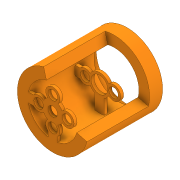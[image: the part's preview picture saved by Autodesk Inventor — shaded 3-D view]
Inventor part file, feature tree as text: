
AUTODESK INVENTOR PART (.ipt)
format: ipt  version: 2020 (Build 240168000, 168)  size: 354,816 bytes
history: native  units: in
note: dims shown in document units (in); Inventor stores cm internally (conversion verified against a paired STEP export)
features: extrude x7, sketch x7, projected_geometry x3, chamfer x1
ambient origin geometry x8: Origin, YZ Plane, XZ Plane, XY Plane, X Axis, Y Axis, Z Axis, Center Point
bodies: Solid1 (feature_tree)
feature tree (18):
  extrude  "Extrusion1"  Depth=2.0472in
  extrude  "Extrusion2"  Depth=1.6535in
  chamfer  "Chamfer1"  Distance=0.5512in
  extrude  "Extrusion3"  Depth=0.2756in
  extrude  "Extrusion4"  Depth=0.2756in TaperAngle=0.0deg
  extrude  "Extrusion5"  Depth=0.315in
  extrude  "Extrusion6"  Depth=0.315in
  extrude  "Extrusion7"  Depth=0.315in
  sketch  "Sketch1"  dims[d0=2.3622in d1=2.0472in]
  sketch  "Sketch2"  dims[d2=0.2756in d3=0.0in d4=1.6535in d5=0.5512in d6=0.0in]
  sketch  "Sketch3"  dims[d7=0.2756in d8=0.125in d9=0.0137in d10=0.0157in]
  sketch  "Sketch5"  dims[d11=4.7244in d13=360.0deg d15=0.2756in d16=0.0in]
  sketch  "Sketch6"  dims[d17=0.5512in d19=0.315in]
  projected_geometry  "Projected Loop1"
  sketch  "Sketch7"  dims[d20=0.315in d21=0.4724in]
  projected_geometry  "Projected Loop2"
  sketch  "Sketch8"  dims[d22=0.4724in d23=0.0787in d24=0.0787in d25=0.0787in d26=0.0984in d27=0.0in d28=0.1575in d29=0.1575in d30=120.0deg d31=15.0deg d32=0.4921in d33=0.0in d34=1.4567in d35=0.0in d36=1.5748in d38=360.0deg d40=0.0787in d41=0.0787in d42=0.0787in d43=0.0787in d44=0.0787in d45=0.0984in d46=0.0in d47=0.315in]
  projected_geometry  "Projected Loop3"
